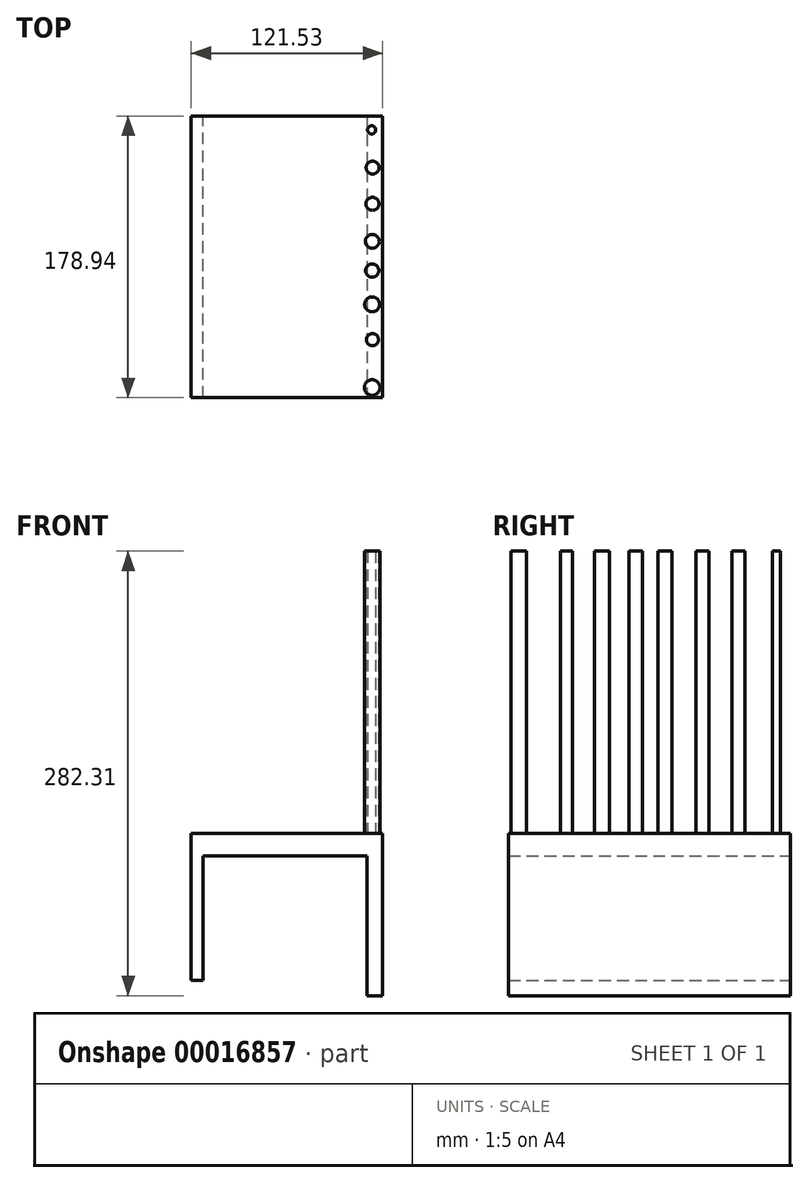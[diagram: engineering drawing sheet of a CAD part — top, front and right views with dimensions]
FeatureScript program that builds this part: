
annotation { "Feature Type Name" : "Feature", "Feature Type Description" : "" }
export const myFeature = defineFeature(function(context is Context, id is Id, definition is map)
    precondition{}
    {
        {
            var Q0;
            Q0=qCreatedBy(makeId("Front.planeOp"),FACE);
            var sketch = newSketch(context, id + "F0", { "sketchPlane" : qUnion([Q0])});
            skLineSegment(sketch, "E0.bottom", {"start": v(-67.25, 40.17) * mm, "end": v(-59.64, 40.17) * mm});
            skLineSegment(sketch, "E0.top", {"start": v(-67.25, -53.38) * mm, "end": v(-59.64, -53.38) * mm});
            skLineSegment(sketch, "E0.left", {"start": v(-67.25, 40.17) * mm, "end": v(-67.25, -53.38) * mm});
            skLineSegment(sketch, "E0.right", {"start": v(-59.64, 40.17) * mm, "end": v(-59.64, -53.38) * mm});
            skSolve(sketch);
        }
        {
            var Q0;
            Q0=makeQuery(id+"F0.imprint","IMPRINT",FACE,{"disambiguationData":[TD([[makeQuery(id+"F0.imprint","IMPRINT",EDGE,{"derivedFrom":sQuery(id+"F0.wireOp",EDGE,"E0.bottom")}),-1.0]])]});
            extrude(context, id + "F1", {"entities" : qUnion([Q0]), "depth" : 88.9 * mm});
        }
        {
            var Q0;
            Q0=makeQuery(id+"F1.opExtrude","SWEPT_FACE",FACE,{"disambiguationData":[OSD([sQuery(id+"F0.wireOp",EDGE,"E0.right")])]});
            var sketch = newSketch(context, id + "F2", { "sketchPlane" : qUnion([Q0])});
            skLineSegment(sketch, "E1.bottom", {"start": v(-88.9, 40.17) * mm, "end": v(0, 40.17) * mm});
            skLineSegment(sketch, "E1.top", {"start": v(-88.9, 25.9) * mm, "end": v(0, 25.9) * mm});
            skLineSegment(sketch, "E1.left", {"start": v(-88.9, 40.17) * mm, "end": v(-88.9, 25.9) * mm});
            skLineSegment(sketch, "E1.right", {"start": v(0, 40.17) * mm, "end": v(0, 25.9) * mm});
            skSolve(sketch);
        }
        {
            var Q0;
            Q0=makeQuery(id+"F2.imprint","IMPRINT",FACE,{"disambiguationData":[TD([[makeQuery(id+"F2.imprint","IMPRINT",EDGE,{"derivedFrom":sQuery(id+"F2.wireOp",EDGE,"E1.bottom")}),-1.0]])]});
            extrude(context, id + "F3", {"entities" : qUnion([Q0]), "operationType" : NewBodyOperationType.ADD, "depth" : 113.93 * mm});
        }
        {
            var Q0;
            Q0=makeQuery(id+"F3.opExtrude","SWEPT_FACE",FACE,{"disambiguationData":[OSD([sQuery(id+"F2.wireOp",EDGE,"E1.top")])]});
            var sketch = newSketch(context, id + "F4", { "sketchPlane" : qUnion([Q0])});
            skLineSegment(sketch, "E2.bottom", {"start": v(56.53, 0) * mm, "end": v(44.32, 0) * mm});
            skLineSegment(sketch, "E2.top", {"start": v(56.53, 88.9) * mm, "end": v(44.32, 88.9) * mm});
            skLineSegment(sketch, "E2.left", {"start": v(56.53, 0) * mm, "end": v(56.53, 88.9) * mm});
            skLineSegment(sketch, "E2.right", {"start": v(44.32, 0) * mm, "end": v(44.32, 88.9) * mm});
            skSolve(sketch);
        }
        {
            var Q0;
            {var subQ2=sQuery(id+"F4.wireOp",EDGE,"E2.right");Q0=makeQuery(id+"F4.imprint","IMPRINT",FACE,{"disambiguationData":[TD([[makeQuery(id+"F4.imprint","IMPRINT",EDGE,{"derivedFrom":subQ2}),-1.0]])]});}
            extrude(context, id + "F5", {"entities" : qUnion([Q0]), "operationType" : NewBodyOperationType.ADD, "depth" : 88.9 * mm});
        }
        {
            var Q0;
            Q0=makeQuery(id+"F5.boolean.opBoolean","MERGE",FACE,{"derivedFrom":[makeQuery(id+"F3.boolean.opBoolean","MERGE",FACE,{"derivedFrom":[makeQuery(id+"F1.opExtrude","CAP_FACE",FACE,{"disambiguationData":[OSD([sQuery(id+"F0.wireOp",EDGE,"E0.bottom"),sQuery(id+"F0.wireOp",EDGE,"E0.top"),sQuery(id+"F0.wireOp",EDGE,"E0.left"),sQuery(id+"F0.wireOp",EDGE,"E0.right")])],"isStart":true}),makeQuery(id+"F3.opExtrude","SWEPT_FACE",FACE,{"disambiguationData":[OSD([sQuery(id+"F2.wireOp",EDGE,"E1.right")])]})]}),makeQuery(id+"F5.opExtrude","SWEPT_FACE",FACE,{"disambiguationData":[OSD([sQuery(id+"F4.wireOp",EDGE,"E2.bottom")])]})]});
            extrude(context, id + "F6", {"entities" : qUnion([Q0]), "operationType" : NewBodyOperationType.ADD, "depth" : 90.04 * mm});
        }
        {
            var Q0;
            {var subQ0=sQuery(id+"F0.wireOp",EDGE,"E0.bottom");var subQ1=sQuery(id+"F2.wireOp",EDGE,"E1.bottom");Q0=makeQuery(id+"F6.boolean.opBoolean","MERGE",FACE,{"derivedFrom":[makeQuery(id+"F3.boolean.opBoolean","MERGE",FACE,{"derivedFrom":[makeQuery(id+"F1.opExtrude","SWEPT_FACE",FACE,{"disambiguationData":[OSD([subQ0])]}),makeQuery(id+"F3.opExtrude","SWEPT_FACE",FACE,{"disambiguationData":[OSD([subQ1])]})]}),makeQuery(id+"F6.opExtrude","SWEPT_FACE",FACE,{"disambiguationData":[OSD([subQ0,subQ1,sQuery(id+"F2.wireOp",EDGE,"E1.right")])]})]});}
            var sketch = newSketch(context, id + "F7", { "sketchPlane" : qUnion([Q0])});
            skCircle(sketch, "E3", {"center": v(47.72, -82.45) * mm, "radius": 4.96 * mm});
            skSolve(sketch);
        }
        {
            var Q0;
            Q0=makeQuery(id+"F7.imprint","IMPRINT",FACE,{"disambiguationData":[TD([[makeQuery(id+"F7.imprint","IMPRINT",EDGE,{"derivedFrom":sQuery(id+"F7.wireOp",EDGE,"E3")}),-1.0]])]});
            var sketch = newSketch(context, id + "F8", { "sketchPlane" : qUnion([Q0])});
            skCircle(sketch, "E4", {"center": v(47.69, -8.14) * mm, "radius": 4.22 * mm});
            skCircle(sketch, "E5", {"center": v(47.77, 10.4) * mm, "radius": 4.42 * mm});
            skCircle(sketch, "E6", {"center": v(47.66, -29.63) * mm, "radius": 4.73 * mm});
            skCircle(sketch, "E7", {"center": v(47.9, -52) * mm, "radius": 3.82 * mm});
            skCircle(sketch, "E8", {"center": v(47.9, 34.25) * mm, "radius": 4.15 * mm});
            skCircle(sketch, "E9", {"center": v(47.98, 57.25) * mm, "radius": 4.1 * mm});
            skCircle(sketch, "E10", {"center": v(47.37, 81.22) * mm, "radius": 2.6 * mm});
            skSolve(sketch);
        }
        {
            var Q0;
            Q0 = qSketchRegion(id + "F8", true);
            var Q1;
            Q1=makeQuery(id+"F7.imprint","IMPRINT",FACE,{"disambiguationData":[TD([[makeQuery(id+"F7.imprint","IMPRINT",EDGE,{"derivedFrom":sQuery(id+"F7.wireOp",EDGE,"E3")}),1.0]])]});
            extrude(context, id + "F9", {"entities" : qUnion([Q0, Q1]), "operationType" : NewBodyOperationType.ADD, "depth" : 179.14 * mm});
        }
    });
